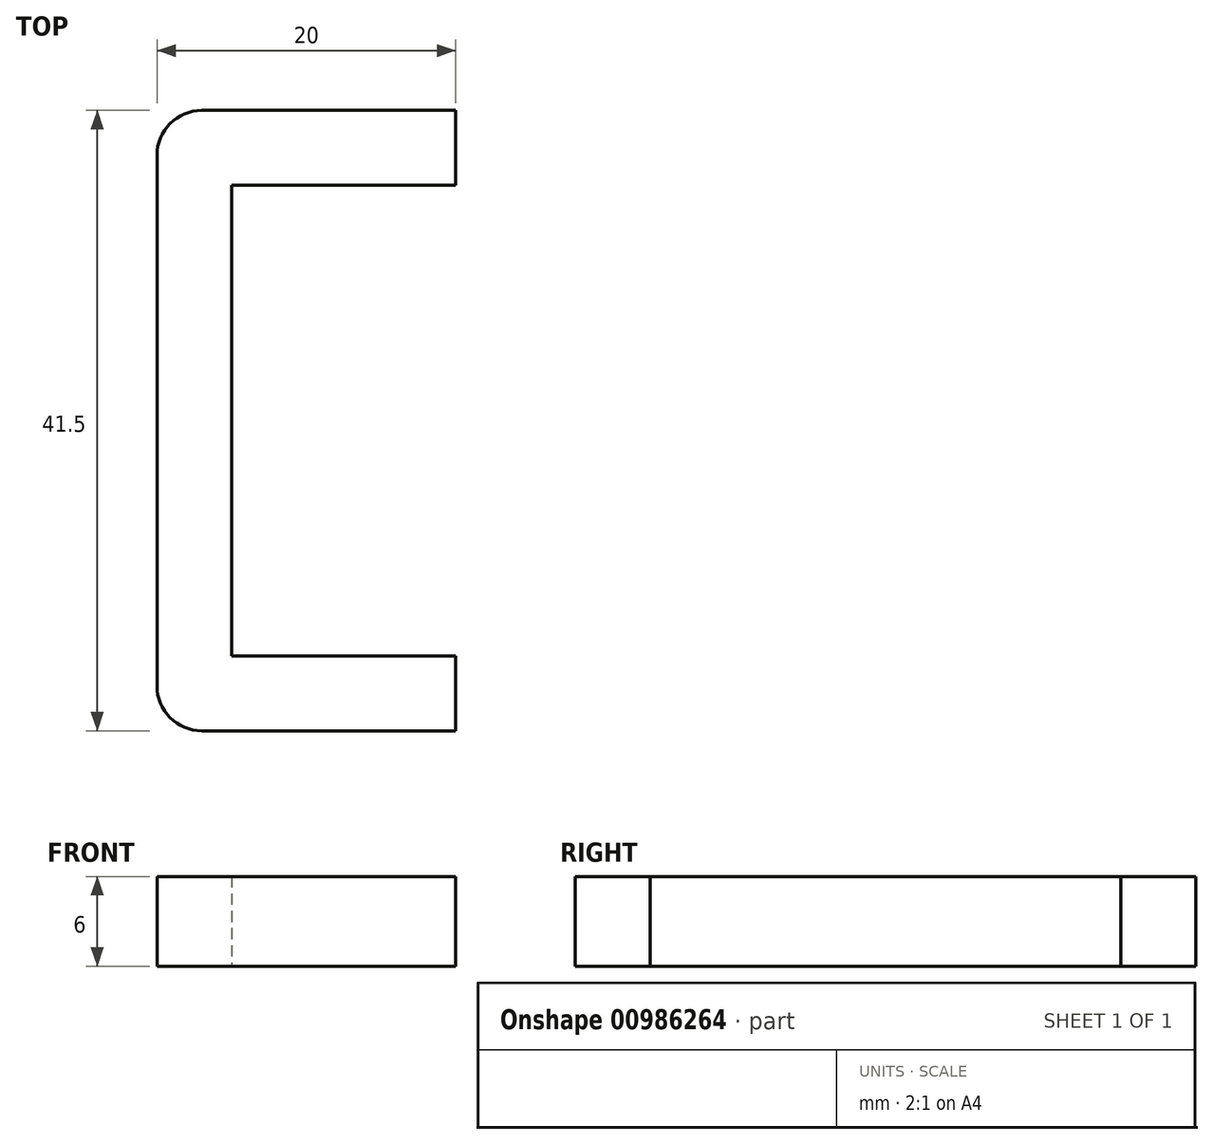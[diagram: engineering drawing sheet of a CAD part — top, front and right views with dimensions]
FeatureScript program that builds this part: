
annotation { "Feature Type Name" : "Feature", "Feature Type Description" : "" }
export const myFeature = defineFeature(function(context is Context, id is Id, definition is map)
    precondition{}
    {
        {
            var Q0;
            Q0=qCreatedBy(makeId("Top.planeOp"),FACE);
            var sketch = newSketch(context, id + "F0", { "sketchPlane" : qUnion([Q0])});
            skLineSegment(sketch, "E0", {"start": v(0, 0) * mm, "end": v(0, 31.5) * mm});
            skLineSegment(sketch, "E1", {"start": v(0, 31.5) * mm, "end": v(15, 31.5) * mm});
            skLineSegment(sketch, "E2", {"start": v(15, 31.5) * mm, "end": v(15, 36.5) * mm});
            skLineSegment(sketch, "E3", {"start": v(15, 36.5) * mm, "end": v(-5, 36.5) * mm});
            skLineSegment(sketch, "E4", {"start": v(-5, 36.5) * mm, "end": v(-5, 0) * mm});
            skLineSegment(sketch, "E5", {"start": v(-5, 0) * mm, "end": v(-5, -5) * mm});
            skLineSegment(sketch, "E6", {"start": v(-5, -5) * mm, "end": v(15, -5) * mm});
            skLineSegment(sketch, "E7", {"start": v(15, -5) * mm, "end": v(15, 0) * mm});
            skLineSegment(sketch, "E8", {"start": v(15, 0) * mm, "end": v(0, 0) * mm});
            skSolve(sketch);
        }
        {
            var Q0;
            Q0=makeQuery(id+"F0.imprint","IMPRINT",FACE,{"disambiguationData":[TD([[makeQuery(id+"F0.imprint","IMPRINT",EDGE,{"derivedFrom":sQuery(id+"F0.wireOp",EDGE,"E0")}),1.0]])]});
            extrude(context, id + "F1", {"entities" : qUnion([Q0]), "depth" : 6 * mm, "offsetDistance" : 25 * mm});
        }
        {
            var Q0;
            Q0=makeQuery(id+"F1.opExtrude","SWEPT_EDGE",EDGE,{"disambiguationData":[OSD([sQuery(id+"F0.wireOp",EDGE,"E3"),sQuery(id+"F0.wireOp",EDGE,"E4")])]});
            var Q1;
            Q1=makeQuery(id+"F1.opExtrude","SWEPT_EDGE",EDGE,{"disambiguationData":[OSD([sQuery(id+"F0.wireOp",EDGE,"E5"),sQuery(id+"F0.wireOp",EDGE,"E6")])]});
            fillet(context, id + "F2", {"entities" : qUnion([Q0, Q1]), "radius" : 3 * mm, "tangentPropagation" : true, "allowEdgeOverflow" : false});
        }
    });
